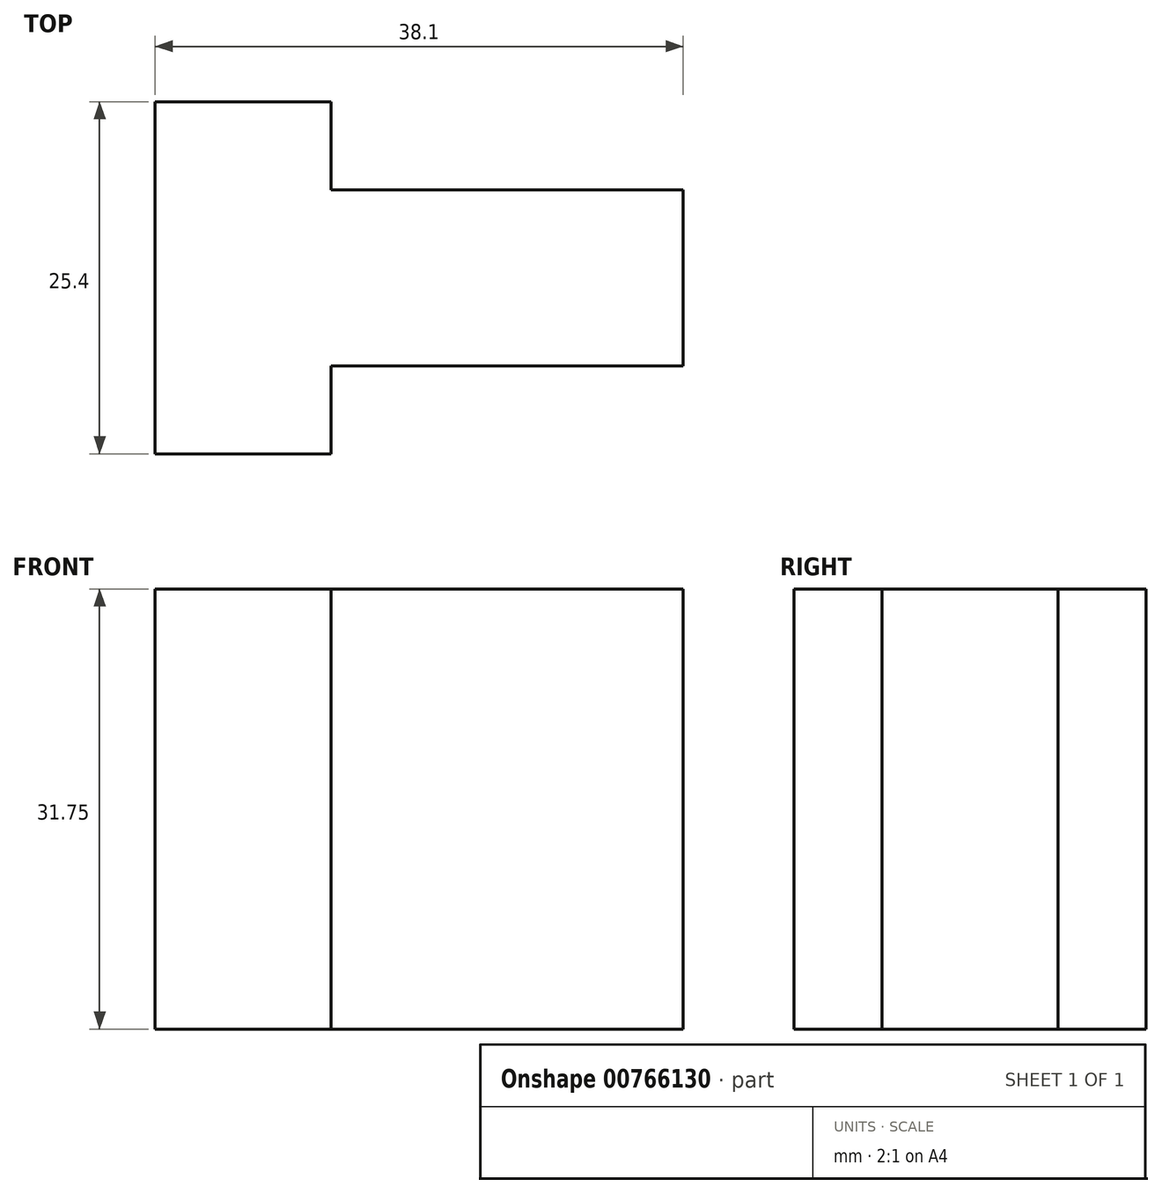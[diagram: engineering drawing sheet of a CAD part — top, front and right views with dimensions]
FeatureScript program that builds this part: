
annotation { "Feature Type Name" : "Feature", "Feature Type Description" : "" }
export const myFeature = defineFeature(function(context is Context, id is Id, definition is map)
    precondition{}
    {
        {
            var Q0;
            Q0=qCreatedBy(makeId("Top.planeOp"),FACE);
            var sketch = newSketch(context, id + "F0", { "sketchPlane" : qUnion([Q0])});
            skLineSegment(sketch, "E0", {"start": v(0, 0) * mm, "end": v(12.7, 0) * mm});
            skLineSegment(sketch, "E1", {"start": v(12.7, 0) * mm, "end": v(12.7, 6.35) * mm});
            skLineSegment(sketch, "E2", {"start": v(12.7, 6.35) * mm, "end": v(38.1, 6.35) * mm});
            skLineSegment(sketch, "E3", {"start": v(38.1, 6.35) * mm, "end": v(38.1, 19.05) * mm});
            skLineSegment(sketch, "E4", {"start": v(38.1, 19.05) * mm, "end": v(12.7, 19.05) * mm});
            skLineSegment(sketch, "E5", {"start": v(12.7, 19.05) * mm, "end": v(12.7, 25.4) * mm});
            skLineSegment(sketch, "E6", {"start": v(12.7, 25.4) * mm, "end": v(0, 25.4) * mm});
            skLineSegment(sketch, "E7", {"start": v(0, 0) * mm, "end": v(0, 25.4) * mm});
            skSolve(sketch);
        }
        {
            var Q0;
            Q0 = qSketchRegion(id + "F0", true);
            extrude(context, id + "F1", {"entities" : qUnion([Q0]), "depth" : 31.75 * mm, "offsetDistance" : 25.4 * mm});
        }
    });
